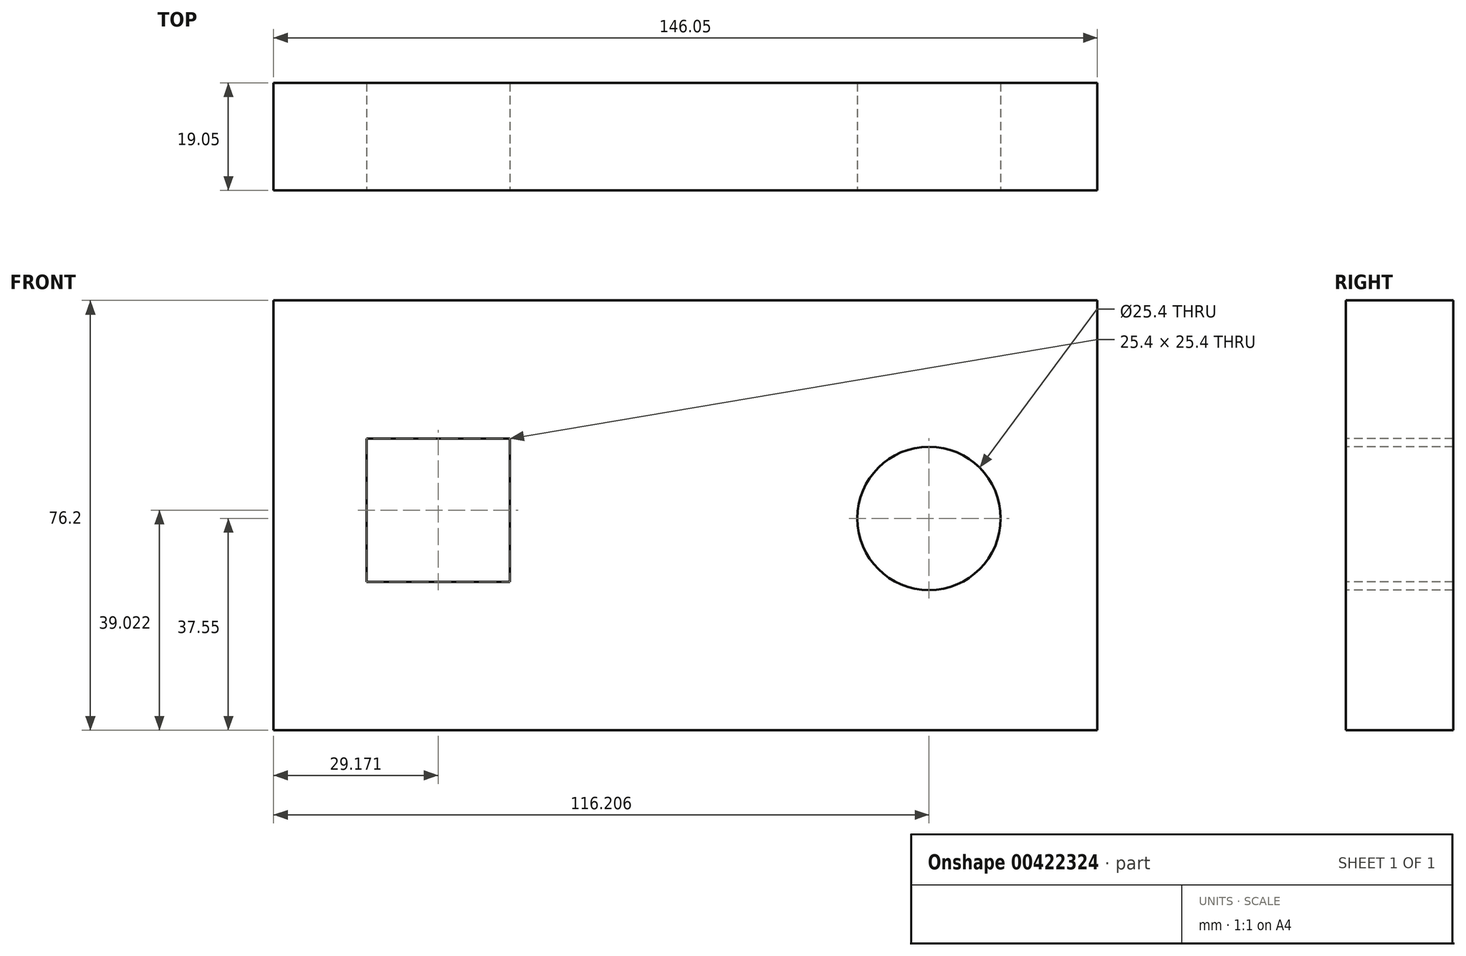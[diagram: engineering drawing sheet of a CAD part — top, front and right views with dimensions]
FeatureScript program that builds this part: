
annotation { "Feature Type Name" : "Feature", "Feature Type Description" : "" }
export const myFeature = defineFeature(function(context is Context, id is Id, definition is map)
    precondition{}
    {
        {
            var Q0;
            Q0=qCreatedBy(makeId("Front.planeOp"),FACE);
            var sketch = newSketch(context, id + "F0", { "sketchPlane" : qUnion([Q0])});
            skLineSegment(sketch, "E0.bottom", {"start": v(-69.5, 38.65) * mm, "end": v(76.55, 38.65) * mm});
            skLineSegment(sketch, "E0.top", {"start": v(-69.5, -37.55) * mm, "end": v(76.55, -37.55) * mm});
            skLineSegment(sketch, "E0.left", {"start": v(-69.5, 38.65) * mm, "end": v(-69.5, -37.55) * mm});
            skLineSegment(sketch, "E0.right", {"start": v(76.55, 38.65) * mm, "end": v(76.55, -37.55) * mm});
            skSolve(sketch);
        }
        {
            var Q0;
            Q0=makeQuery(id+"F0.imprint","IMPRINT",FACE,{"disambiguationData":[TD([[makeQuery(id+"F0.imprint","IMPRINT",EDGE,{"derivedFrom":sQuery(id+"F0.wireOp",EDGE,"E0.bottom")}),-1.0]])]});
            extrude(context, id + "F1", {"entities" : qUnion([Q0]), "depth" : 19.05 * mm});
        }
        {
            var Q0;
            Q0=makeQuery(id+"F1.opExtrude","CAP_FACE",FACE,{"disambiguationData":[OSD([sQuery(id+"F0.wireOp",EDGE,"E0.bottom"),sQuery(id+"F0.wireOp",EDGE,"E0.top"),sQuery(id+"F0.wireOp",EDGE,"E0.left"),sQuery(id+"F0.wireOp",EDGE,"E0.right")])],"isStart":false});
            var sketch = newSketch(context, id + "F2", { "sketchPlane" : qUnion([Q0])});
            skLineSegment(sketch, "E1", {"start": v(-53.03, 14.17) * mm, "end": v(-53.03, -11.23) * mm});
            skLineSegment(sketch, "E2", {"start": v(-53.03, 14.17) * mm, "end": v(-27.63, 14.17) * mm});
            skLineSegment(sketch, "E3", {"start": v(-27.63, 14.17) * mm, "end": v(-27.63, -11.23) * mm});
            skLineSegment(sketch, "E4", {"start": v(-53.03, -11.23) * mm, "end": v(-27.63, -11.23) * mm});
            skSolve(sketch);
        }
        {
            var Q0;
            Q0=makeQuery(id+"F2.imprint","IMPRINT",FACE,{"disambiguationData":[TD([[makeQuery(id+"F2.imprint","IMPRINT",EDGE,{"derivedFrom":sQuery(id+"F2.wireOp",EDGE,"E1")}),1.0]])]});
            extrude(context, id + "F3", {"entities" : qUnion([Q0]), "operationType" : NewBodyOperationType.REMOVE, "oppositeDirection" : true, "depth" : 19.05 * mm});
        }
        {
            var Q0;
            Q0=makeQuery(id+"F1.opExtrude","CAP_FACE",FACE,{"disambiguationData":[OSD([sQuery(id+"F0.wireOp",EDGE,"E0.bottom"),sQuery(id+"F0.wireOp",EDGE,"E0.top"),sQuery(id+"F0.wireOp",EDGE,"E0.left"),sQuery(id+"F0.wireOp",EDGE,"E0.right")])],"isStart":false});
            var sketch = newSketch(context, id + "F4", { "sketchPlane" : qUnion([Q0])});
            skCircle(sketch, "E5", {"center": v(46.7, 0) * mm, "radius": 12.7 * mm});
            skSolve(sketch);
        }
        {
            var Q0;
            Q0=makeQuery(id+"F4.imprint","IMPRINT",FACE,{"disambiguationData":[TD([[makeQuery(id+"F4.imprint","IMPRINT",EDGE,{"derivedFrom":sQuery(id+"F4.wireOp",EDGE,"E5")}),1.0]])]});
            extrude(context, id + "F5", {"entities" : qUnion([Q0]), "operationType" : NewBodyOperationType.REMOVE, "oppositeDirection" : true, "depth" : 19.05 * mm});
        }
    });
